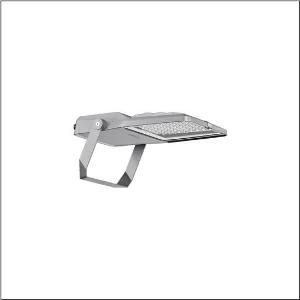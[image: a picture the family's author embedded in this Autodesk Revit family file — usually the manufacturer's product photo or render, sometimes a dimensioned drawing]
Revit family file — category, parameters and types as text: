
# Revit family: floodlight_fl_21_iq_mini___pl64_5xa7772b2e1a_9a08
name_source: partatom
category: Lighting Fixtures
units: mm (PartAtom-declared; Revit-internal decimal feet)

## family parameters
Cut with Voids When Loaded = No
Host = Face
Light Source = No
Part Type = Normal
Room Calculation Point = No
Round Connector Dimension = Use Diameter
Shared = No

## types (1)
- --- (1 x LED, 6020 lm, 45.5 W, 3000K)
    Apparent Load = 46 VA
    CIE Flux Codes = 28 80 98 100 100
    Color Rendering = 70
    Color Temperature = 3000K
    Default Elevation = 1800 mm
    Description = Floodlight FL 21 iQ mini, floodlight, primary light control with lens, of PMMA, primary optical cover: protective disc, of toughened safety glass, transparent, light distribution: PL64, light emission: direct distribution, installation type: surface-mounted, lamps: LED, High Power LED, rated values: 6.020lm | 45,5W | 132,3lm/W (begin service life); end service life: 6.020lm | 48W; at 50% lumin. flux: 3.010lm | 21,5W | 140lm/W, colour temperature: 3000K, colour rendering: CRI > 70, light colour: 730, light setting 1 begin service life: 100% | 6.020lm | 45,5W | 132,3lm/W | 3.000K, light setting 1 end service life: 48W, further light settings possible, control: Street-Remote, Auto-Match, Temp-Guard, Night-Set, Smart-Wire, Desk-Remote (wireless, voltage-free reading and setting of iQ features in the workshop via application-optimized NFC function/RFID function), optimised constant luminous flux control (CLO 2.0), pre-setting: linear dimming characteristic, with terminal, 6-pole, mains connection: 220..240V, AC, 50/60Hz, luminaire housing, of diecast aluminium, powder-coated, SITECO metallic grey (DB 702S), corrosivity category C5 mid according to DIN EN ISO 12944suitable for swimming poolschlorine-resistant, sealing non-destructively replaceable, mounting bracket, of steel, galvanised, powder-coated, SITECO metallic grey (DB 702S), protection rating (complete): IP66, insulation class (complete): insulation class II (safety insulation), certification: CE, ENEC, VDE, protection symbol: D, impact resistance: IK08, permissible operating ambient temperature: -40..+40°C, permissible operating ambient temperature for outdoor applications: -40..+50°C, standard: DIN EN 12944, LABS conformity tested according to VDMA 24364:2018-05, packaging unit: 1 piece

Light Distribution: PL64
    Height = 70 mm
    Lamp = 1 x LED
    Lamp Light Flux = 6020 lm
    Lamp Power = 45.5 W
    Lamp count = 1
    Length = 485 mm
    Luminous efficacy = 132 lm/W
    Manufacturer = Siteco
    ModVariant = No
    Model = 5XA7772B2E1A
    Mounting Place = Pole
    Mounting Type = Pole annexe
    Number of Poles = 1
    OnlyDefault = Yes
    Power Factor = 1
    Product Name = Floodlight FL 21 iQ mini | PL64
    Product group = floodlight | pylon annexe
    ProductGroupID = 6201
    Protection Class = Protection class II
    Protection Degree = IP 66
    RLX_Detail_Level = 1
    RLX_Emergency_Light_Flux = 0 lm
    RLX_Emergency_Type = 0
    RLX_Emergency_Type_DB = No
    RlxData = <blob elided: 96429 chars, md5=9fa11771>
    Socket = socket
    Standby Power = 0 W
    System Light Flux = 6020 lm
    System Power = 46 W
    Type Comments = factory setting: luminous flux: 100 % | dim-lin: 254 | 463 mA
    Type Image = l_1006845.jpg
    URL = http://relux.com
    VarID = @adj_168007
    Voltage = 0 V
    Weight = 0.00 kg
    Width = 337 mm

## geometry (parser evidence)
native form markers: Blend x4, Sweep x11
no freeform markers — native parametric forms only
